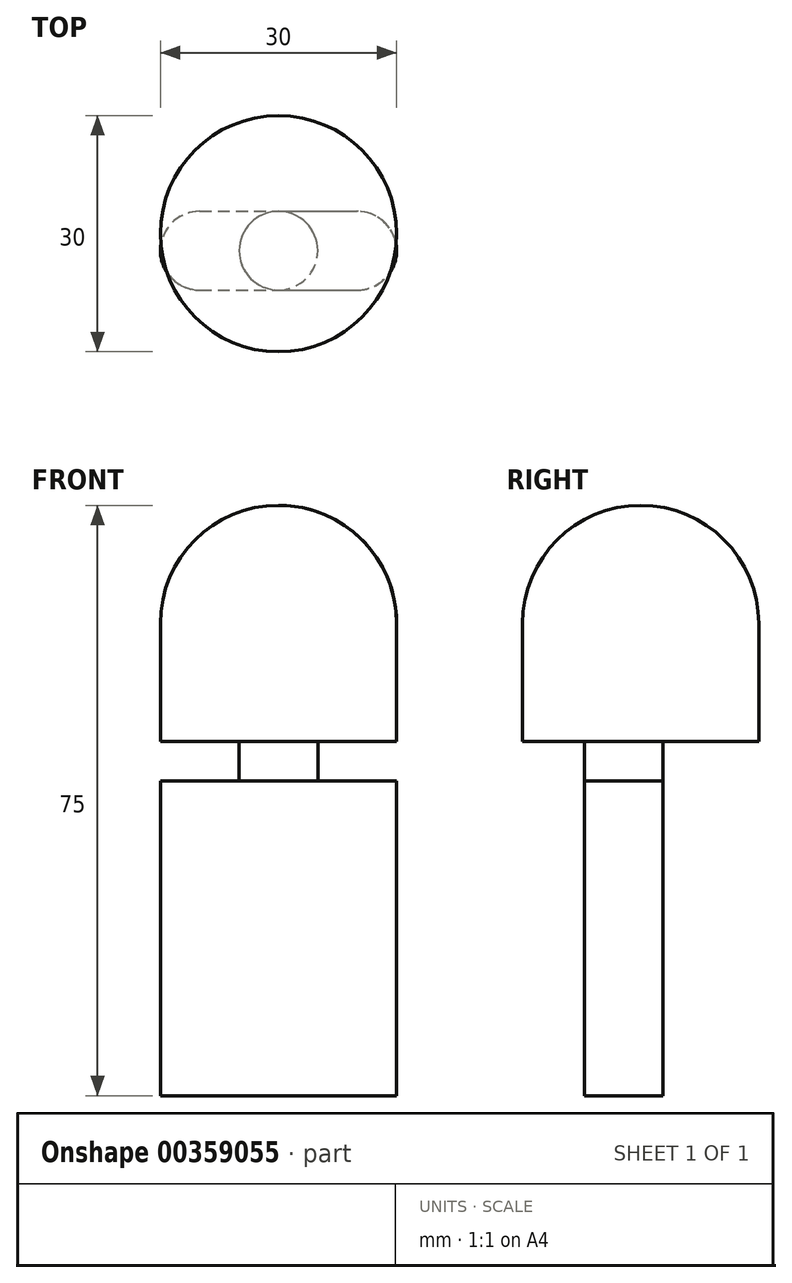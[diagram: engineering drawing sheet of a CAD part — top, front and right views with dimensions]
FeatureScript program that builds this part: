
annotation { "Feature Type Name" : "Feature", "Feature Type Description" : "" }
export const myFeature = defineFeature(function(context is Context, id is Id, definition is map)
    precondition{}
    {
        {
            var Q0;
            Q0=qCreatedBy(makeId("Right.planeOp"),FACE);
            var sketch = newSketch(context, id + "F0", { "sketchPlane" : qUnion([Q0])});
            skLineSegment(sketch, "E0.bottom", {"start": v(0, 0) * mm, "end": v(10, 0) * mm});
            skLineSegment(sketch, "E0.top", {"start": v(0, 40) * mm, "end": v(10, 40) * mm});
            skLineSegment(sketch, "E0.left", {"start": v(0, 0) * mm, "end": v(0, 40) * mm});
            skLineSegment(sketch, "E0.right", {"start": v(10, 0) * mm, "end": v(10, 40) * mm});
            skSolve(sketch);
        }
        {
            var Q0;
            Q0 = qSketchRegion(id + "F0", true);
            extrude(context, id + "F1", {"entities" : qUnion([Q0]), "oppositeDirection" : true, "depth" : 30 * mm});
        }
        {
            var Q0;
            Q0=makeQuery(id+"F1.opExtrude","CAP_EDGE",EDGE,{"disambiguationData":[OSD([sQuery(id+"F0.wireOp",EDGE,"E0.right")])],"isStart":true});
            var Q1;
            Q1=makeQuery(id+"F1.opExtrude","CAP_EDGE",EDGE,{"disambiguationData":[OSD([sQuery(id+"F0.wireOp",EDGE,"E0.left")])],"isStart":true});
            var Q2;
            Q2=makeQuery(id+"F1.opExtrude","CAP_EDGE",EDGE,{"disambiguationData":[OSD([sQuery(id+"F0.wireOp",EDGE,"E0.right")])],"isStart":false});
            var Q3;
            Q3=makeQuery(id+"F1.opExtrude","CAP_EDGE",EDGE,{"disambiguationData":[OSD([sQuery(id+"F0.wireOp",EDGE,"E0.left")])],"isStart":false});
            fillet(context, id + "F2", {"entities" : qUnion([Q0, Q1, Q2, Q3]), "radius" : 5 * mm, "tangentPropagation" : true, "allowEdgeOverflow" : false});
        }
        {
            var Q0;
            Q0=makeQuery(id+"F1.opExtrude","SWEPT_FACE",FACE,{"disambiguationData":[OSD([sQuery(id+"F0.wireOp",EDGE,"E0.top")])]});
            var sketch = newSketch(context, id + "F3", { "sketchPlane" : qUnion([Q0])});
            skCircle(sketch, "E1", {"center": v(-15, 5) * mm, "radius": 5 * mm});
            skPoint(sketch, "E1.centerSnap0", {"position": v(-15, 0) * mm});
            skSolve(sketch);
        }
        {
            var Q0;
            Q0 = qSketchRegion(id + "F3", true);
            extrude(context, id + "F4", {"entities" : qUnion([Q0]), "operationType" : NewBodyOperationType.ADD, "depth" : 5 * mm});
        }
        {
            var Q0;
            Q0=makeQuery(id+"F4.opExtrude","CAP_FACE",FACE,{"disambiguationData":[OSD([sQuery(id+"F3.wireOp",EDGE,"E1")])],"isStart":false});
            var sketch = newSketch(context, id + "F5", { "sketchPlane" : qUnion([Q0])});
            skLineSegment(sketch, "E2.bottom", {"start": v(-30, -7.84) * mm, "end": v(0, -7.84) * mm});
            skLineSegment(sketch, "E2.top", {"start": v(-30, 22.16) * mm, "end": v(0, 22.16) * mm});
            skLineSegment(sketch, "E2.left", {"start": v(-30, -7.84) * mm, "end": v(-30, 22.16) * mm});
            skLineSegment(sketch, "E2.right", {"start": v(0, -7.84) * mm, "end": v(0, 22.16) * mm});
            skSolve(sketch);
        }
        {
            var Q0;
            Q0 = qSketchRegion(id + "F5", true);
            extrude(context, id + "F6", {"entities" : qUnion([Q0]), "operationType" : NewBodyOperationType.ADD, "depth" : 30 * mm});
        }
        {
            var Q0;
            Q0=makeQuery(id+"F6.opExtrude","CAP_FACE",FACE,{"disambiguationData":[OSD([sQuery(id+"F5.wireOp",EDGE,"E2.bottom"),sQuery(id+"F5.wireOp",EDGE,"E2.top"),sQuery(id+"F5.wireOp",EDGE,"E2.left"),sQuery(id+"F5.wireOp",EDGE,"E2.right")])],"isStart":false});
            var Q1;
            Q1=makeQuery(id+"F6.opExtrude","SWEPT_EDGE",EDGE,{"disambiguationData":[OSD([sQuery(id+"F5.wireOp",EDGE,"E2.top"),sQuery(id+"F5.wireOp",EDGE,"E2.left")])]});
            var Q2;
            Q2=makeQuery(id+"F6.opExtrude","SWEPT_EDGE",EDGE,{"disambiguationData":[OSD([sQuery(id+"F5.wireOp",EDGE,"E2.top"),sQuery(id+"F5.wireOp",EDGE,"E2.right")])]});
            var Q3;
            Q3=makeQuery(id+"F6.opExtrude","SWEPT_EDGE",EDGE,{"disambiguationData":[OSD([sQuery(id+"F5.wireOp",EDGE,"E2.bottom"),sQuery(id+"F5.wireOp",EDGE,"E2.right")])]});
            var Q4;
            Q4=makeQuery(id+"F6.opExtrude","SWEPT_EDGE",EDGE,{"disambiguationData":[OSD([sQuery(id+"F5.wireOp",EDGE,"E2.bottom"),sQuery(id+"F5.wireOp",EDGE,"E2.left")])]});
            fillet(context, id + "F7", {"entities" : qUnion([Q0, Q1, Q2, Q3, Q4]), "radius" : 15 * mm, "tangentPropagation" : true, "allowEdgeOverflow" : false});
        }
    });
